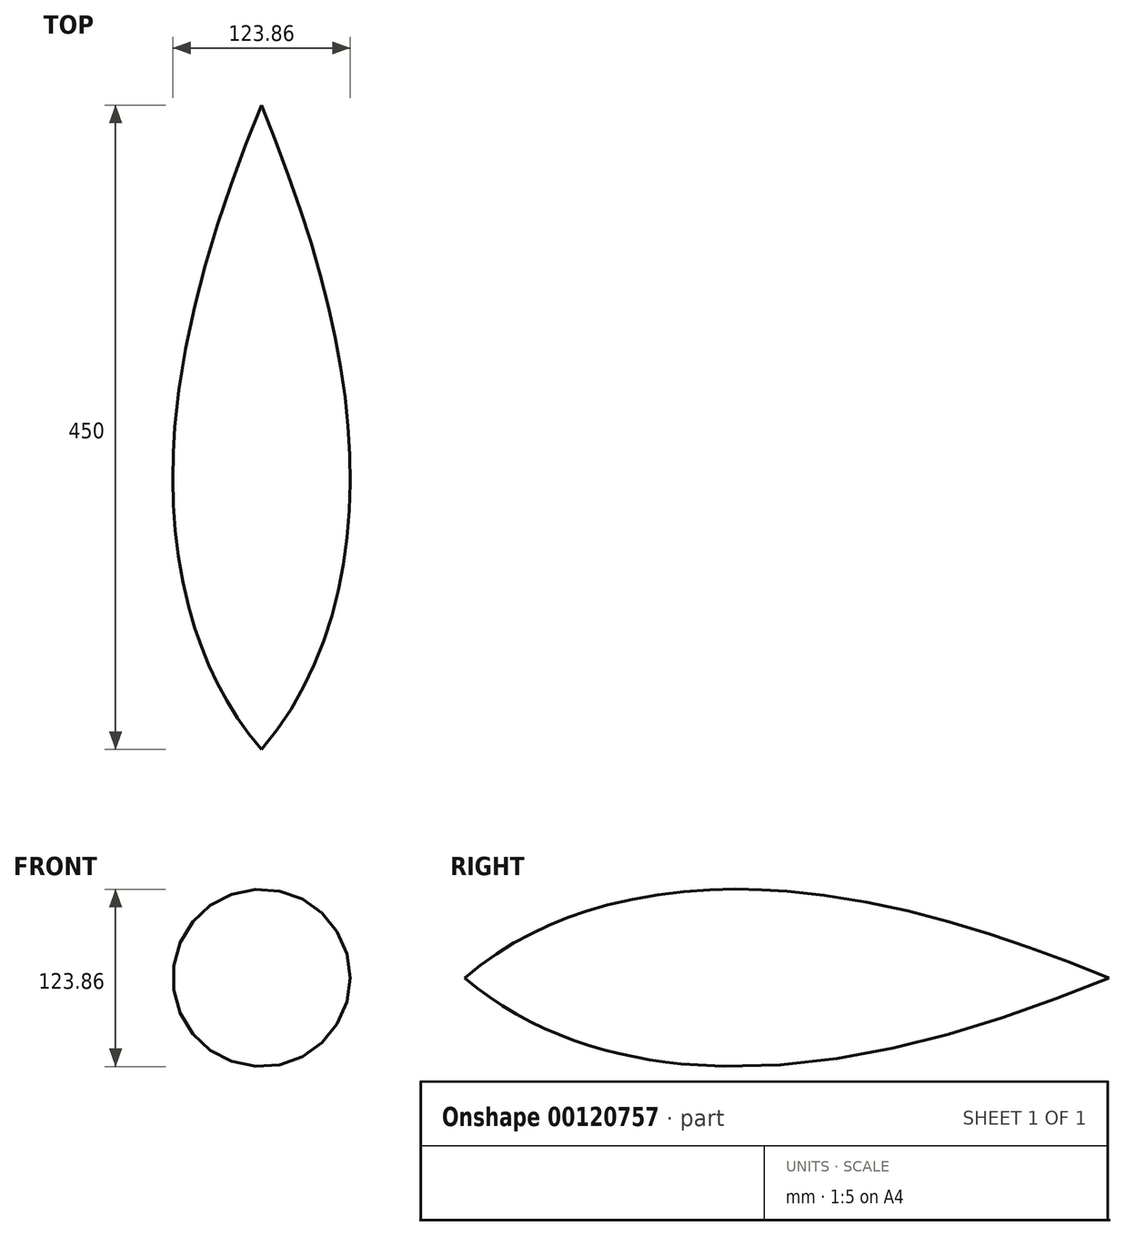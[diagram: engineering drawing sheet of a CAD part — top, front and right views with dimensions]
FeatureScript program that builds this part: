
annotation { "Feature Type Name" : "Feature", "Feature Type Description" : "" }
export const myFeature = defineFeature(function(context is Context, id is Id, definition is map)
    precondition{}
    {
        {
            var Q0;
            Q0=qCreatedBy(makeId("Top.planeOp"),FACE);
            var sketch = newSketch(context, id + "F0", { "sketchPlane" : qUnion([Q0])});
            skFitSpline(sketch, "E0", {"points": [v(0, -170.88) * mm, v(61.47, 0) * mm, v(0, 279.12) * mm], "startDerivative": vector(263.87, 305.14) * mm, "endDerivative": vector(-237.08, 580.15) * mm});
            skLineSegment(sketch, "E1", {"start": v(0, -170.88) * mm, "end": v(0, 279.12) * mm, "construction": true});
            skLineSegment(sketch, "E2", {"start": v(0, -170.88) * mm, "end": v(0, 279.12) * mm});
            skSolve(sketch);
        }
        {
            var Q0;
            Q0 = qSketchRegion(id + "F0", true);
            var Q1;
            Q1=sQuery(id+"F0.wireOp",EDGE,"E1");
            revolve(context, id + "F1", {"entities" : qUnion([Q0]), "axis" : qUnion([Q1]), "revolveType" : RevolveType.FULL});
        }
    });
